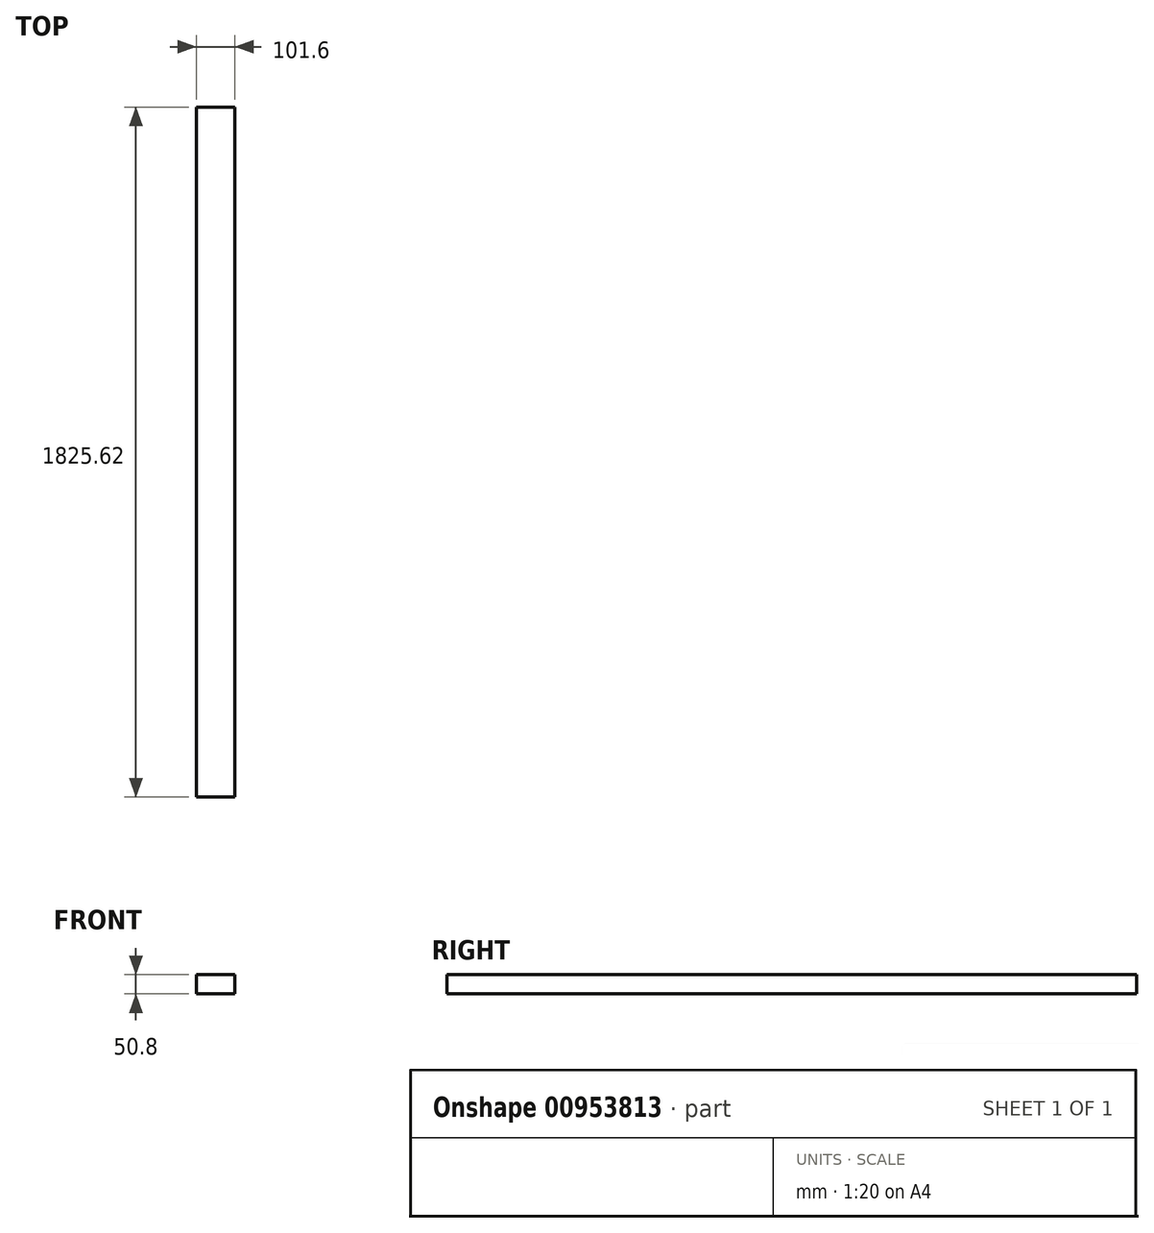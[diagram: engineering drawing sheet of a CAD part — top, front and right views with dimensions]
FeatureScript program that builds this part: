
annotation { "Feature Type Name" : "Feature", "Feature Type Description" : "" }
export const myFeature = defineFeature(function(context is Context, id is Id, definition is map)
    precondition{}
    {
        {
            var Q0;
            Q0=qCreatedBy(makeId("Front.planeOp"),FACE);
            var sketch = newSketch(context, id + "F0", { "sketchPlane" : qUnion([Q0])});
            skLineSegment(sketch, "E0.bottom", {"start": v(-50.8, -25.4) * mm, "end": v(50.8, -25.4) * mm});
            skLineSegment(sketch, "E0.top", {"start": v(-50.8, 25.4) * mm, "end": v(50.8, 25.4) * mm});
            skLineSegment(sketch, "E0.left", {"start": v(-50.8, -25.4) * mm, "end": v(-50.8, 25.4) * mm});
            skLineSegment(sketch, "E0.right", {"start": v(50.8, -25.4) * mm, "end": v(50.8, 25.4) * mm});
            skPoint(sketch, "E0.middle", {"position": v(0, 0) * mm});
            skSolve(sketch);
        }
        {
            var Q0;
            Q0 = qSketchRegion(id + "F0", true);
            extrude(context, id + "F1", {"entities" : qUnion([Q0]), "depth" : 1825.62 * mm, "offsetDistance" : 25.4 * mm});
        }
    });
